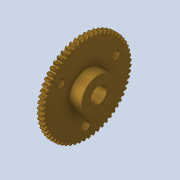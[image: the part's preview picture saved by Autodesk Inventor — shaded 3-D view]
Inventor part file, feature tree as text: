
AUTODESK INVENTOR PART (.ipt)
format: ipt  version: 2020.4 (Build 244396000, 396)  size: 613,376 bytes
history: native  units: mm
features: extrude x2, sketch x2, other x1, pattern_circular x1
ambient origin geometry x8: Origin, YZ Plane, XZ Plane, XY Plane, X Axis, Y Axis, Z Axis, Center Point
bodies: Body1 (feature_tree)
feature tree (6):
  other  "Sólido1"
  extrude  "Thread Entrance"  Depth=11.0mm
  pattern_circular  "Circular Pattern1"  [2 undecoded]
  extrude  "Hole Machined"  Depth=10.0mm
  sketch  "Sketch3"  dims[d9=3.0mm d10=11.0mm]
  sketch  "Sketch4"  dims[d11=0.0mm d12=10.0mm d13=0.0mm d14=30.0mm d15=62.831853mm d17=5.5mm d18=10.0mm d19=0.0mm]
note: 2 required parameter values undecoded (feature->parameter linkage not recoverable at this tier; creation-order binding heuristic only, values carry confidence <= 0.55)
